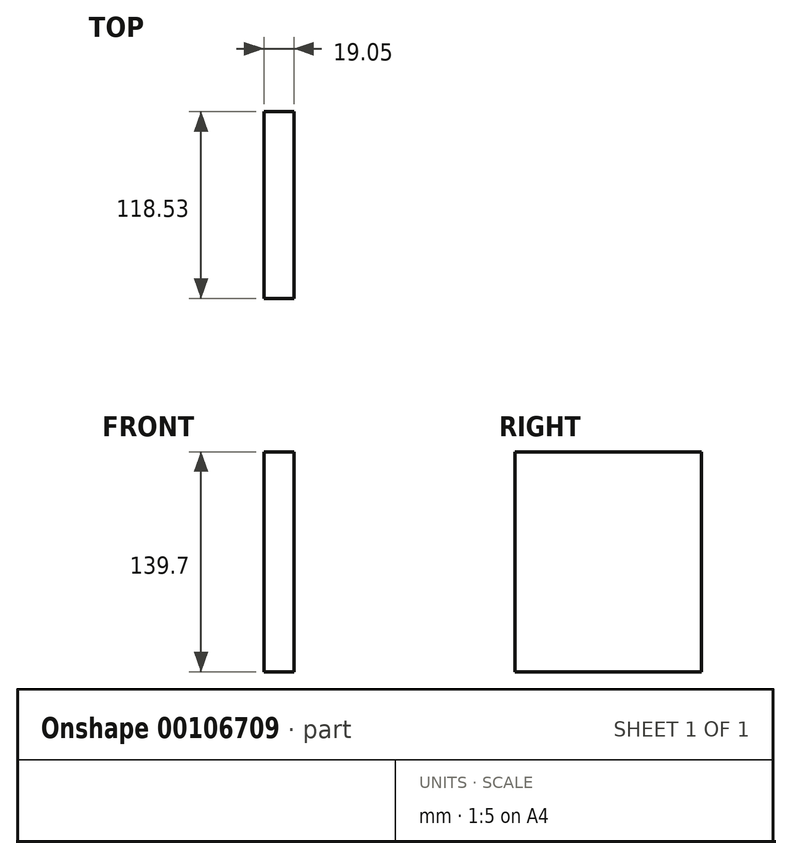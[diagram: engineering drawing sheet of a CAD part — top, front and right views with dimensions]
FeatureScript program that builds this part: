
annotation { "Feature Type Name" : "Feature", "Feature Type Description" : "" }
export const myFeature = defineFeature(function(context is Context, id is Id, definition is map)
    precondition{}
    {
        {
            var Q0;
            Q0=qCreatedBy(makeId("Right.planeOp"),FACE);
            var sketch = newSketch(context, id + "F0", { "sketchPlane" : qUnion([Q0])});
            skLineSegment(sketch, "E0.bottom", {"start": v(0, 0) * mm, "end": v(118.53, 0) * mm});
            skLineSegment(sketch, "E0.top", {"start": v(0, 139.7) * mm, "end": v(118.53, 139.7) * mm});
            skLineSegment(sketch, "E0.left", {"start": v(0, 0) * mm, "end": v(0, 139.7) * mm});
            skLineSegment(sketch, "E0.right", {"start": v(118.53, 0) * mm, "end": v(118.53, 139.7) * mm});
            skSolve(sketch);
        }
        {
            var Q0;
            Q0=makeQuery(id+"F0.imprint","IMPRINT",FACE,{"disambiguationData":[TD([[makeQuery(id+"F0.imprint","IMPRINT",EDGE,{"derivedFrom":sQuery(id+"F0.wireOp",EDGE,"E0.bottom")}),1.0]])]});
            extrude(context, id + "F1", {"entities" : qUnion([Q0]), "depth" : 19.05 * mm});
        }
    });
